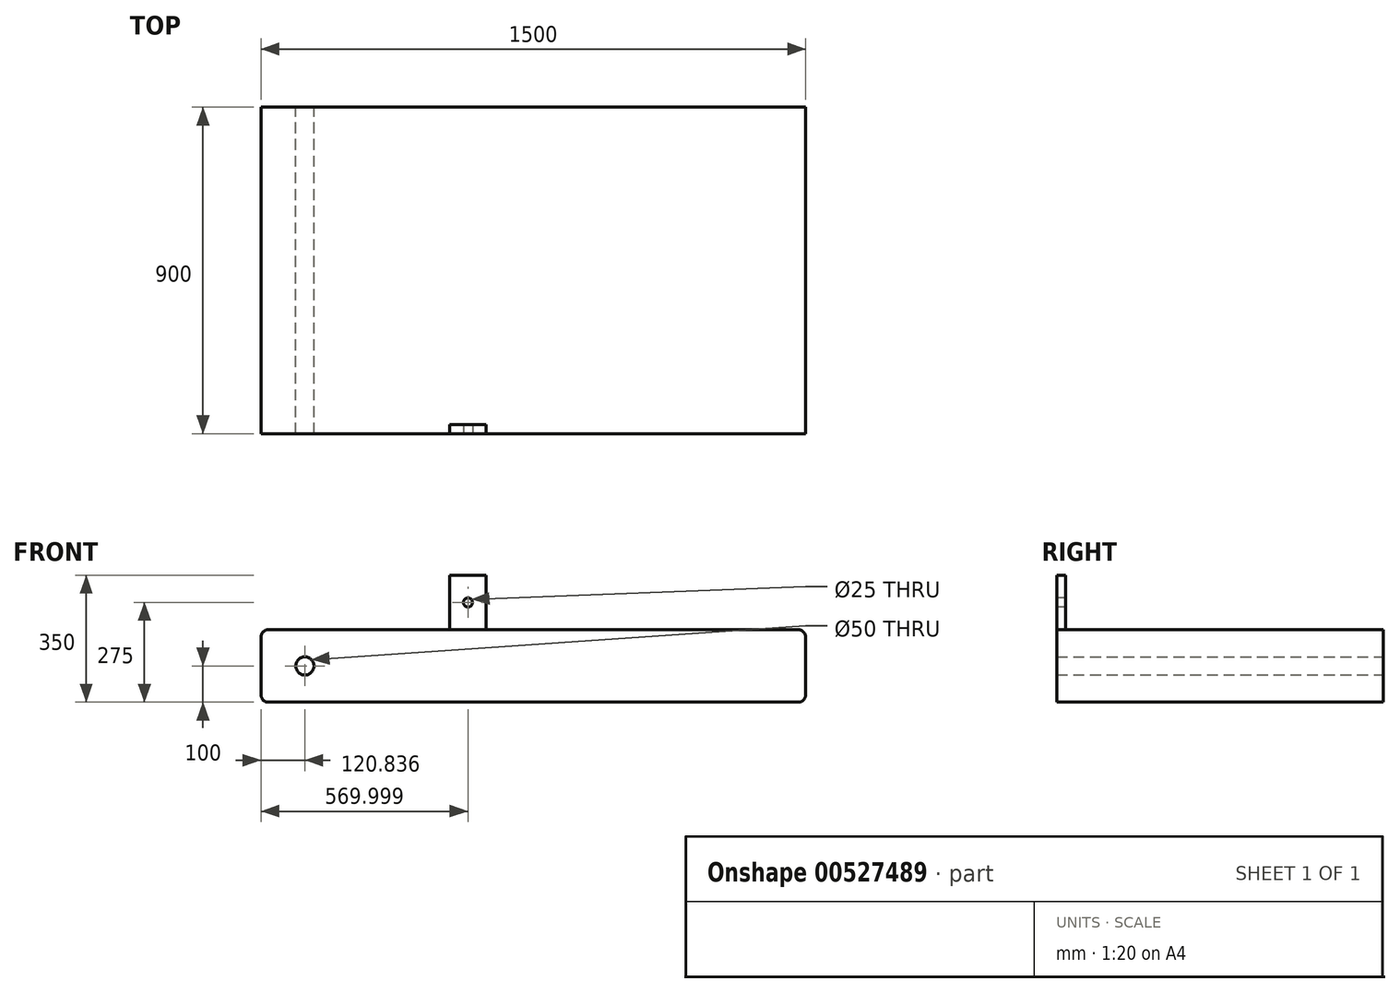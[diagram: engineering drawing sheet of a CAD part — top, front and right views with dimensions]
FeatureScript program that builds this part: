
annotation { "Feature Type Name" : "Feature", "Feature Type Description" : "" }
export const myFeature = defineFeature(function(context is Context, id is Id, definition is map)
    precondition{}
    {
        {
            var Q0;
            Q0=qCreatedBy(makeId("Front.planeOp"),FACE);
            var sketch = newSketch(context, id + "F0", { "sketchPlane" : qUnion([Q0])});
            skLineSegment(sketch, "E0.bottom", {"start": v(-939.18, 0) * mm, "end": v(560.82, 0) * mm});
            skLineSegment(sketch, "E0.top", {"start": v(-939.18, 200) * mm, "end": v(560.82, 200) * mm});
            skLineSegment(sketch, "E0.left", {"start": v(-939.18, 0) * mm, "end": v(-939.18, 200) * mm});
            skLineSegment(sketch, "E0.right", {"start": v(560.82, 0) * mm, "end": v(560.82, 200) * mm});
            skLineSegment(sketch, "E1", {"start": v(-939.18, 100) * mm, "end": v(560.82, 100) * mm, "construction": true});
            skPoint(sketch, "E2", {"position": v(-818.34, 100) * mm});
            skSolve(sketch);
        }
        {
            var Q0;
            Q0 = qSketchRegion(id + "F0", true);
            extrude(context, id + "F1", {"entities" : qUnion([Q0]), "depth" : 900 * mm, "offsetDistance" : 25 * mm});
        }
        {
            var Q0;
            Q0=sQuery(id+"F0.wireOp",VERTEX,"E2");
            var Q1;
            Q1=makeQuery(id+"F1.opExtrude","SWEPT_BODY",BODY,{"disambiguationData":[OSD([sQuery(id+"F0.wireOp",EDGE,"E0.bottom"),sQuery(id+"F0.wireOp",EDGE,"E0.top"),sQuery(id+"F0.wireOp",EDGE,"E0.left"),sQuery(id+"F0.wireOp",EDGE,"E0.right")])]});
            hole(context, id + "F2", {"style" : HoleStyle.SIMPLE, "endStyle" : HoleEndStyle.THROUGH, "oppositeDirection" : true, "holeDiameter" : 50 * mm, "isTappedThrough" : true, "tappedDepth" : 12 * mm, "tapClearance" : 3, "locations" : qUnion([Q0]), "scope" : qUnion([Q1])});
        }
        {
            var Q0;
            Q0=makeQuery(id+"F1.opExtrude","SWEPT_EDGE",EDGE,{"disambiguationData":[OSD([sQuery(id+"F0.wireOp",EDGE,"E0.top"),sQuery(id+"F0.wireOp",EDGE,"E0.left")])]});
            var Q1;
            Q1=makeQuery(id+"F1.opExtrude","SWEPT_EDGE",EDGE,{"disambiguationData":[OSD([sQuery(id+"F0.wireOp",EDGE,"E0.bottom"),sQuery(id+"F0.wireOp",EDGE,"E0.left")])]});
            var Q2;
            Q2=makeQuery(id+"F1.opExtrude","SWEPT_EDGE",EDGE,{"disambiguationData":[OSD([sQuery(id+"F0.wireOp",EDGE,"E0.top"),sQuery(id+"F0.wireOp",EDGE,"E0.right")])]});
            var Q3;
            Q3=makeQuery(id+"F1.opExtrude","SWEPT_EDGE",EDGE,{"disambiguationData":[OSD([sQuery(id+"F0.wireOp",EDGE,"E0.bottom"),sQuery(id+"F0.wireOp",EDGE,"E0.right")])]});
            fillet(context, id + "F3", {"entities" : qUnion([Q0, Q1, Q2, Q3]), "radius" : 20 * mm, "tangentPropagation" : true, "allowEdgeOverflow" : false});
        }
        {
            var Q0;
            Q0=makeQuery(id+"F1.opExtrude","CAP_FACE",FACE,{"disambiguationData":[OSD([sQuery(id+"F0.wireOp",EDGE,"E0.bottom"),sQuery(id+"F0.wireOp",EDGE,"E0.top"),sQuery(id+"F0.wireOp",EDGE,"E0.left"),sQuery(id+"F0.wireOp",EDGE,"E0.right")])],"isStart":false});
            var sketch = newSketch(context, id + "F4", { "sketchPlane" : qUnion([Q0])});
            skLineSegment(sketch, "E3.bottom", {"start": v(-319.18, 350) * mm, "end": v(-419.18, 350) * mm});
            skLineSegment(sketch, "E3.top", {"start": v(-319.18, 200) * mm, "end": v(-419.18, 200) * mm});
            skLineSegment(sketch, "E3.left", {"start": v(-319.18, 350) * mm, "end": v(-319.18, 200) * mm});
            skLineSegment(sketch, "E3.right", {"start": v(-419.18, 350) * mm, "end": v(-419.18, 200) * mm});
            skPoint(sketch, "E4.positionSnap0", {"position": v(-369.18, 350) * mm});
            skPoint(sketch, "E4.positionSnap1", {"position": v(-319.18, 275) * mm});
            skCircle(sketch, "E5", {"center": v(-369.18, 275) * mm, "radius": 12.5 * mm});
            skSolve(sketch);
        }
        {
            var Q0;
            Q0 = qSketchRegion(id + "F4", true);
            extrude(context, id + "F5", {"entities" : qUnion([Q0]), "oppositeDirection" : true, "depth" : 25 * mm, "offsetDistance" : 25 * mm});
        }
    });
